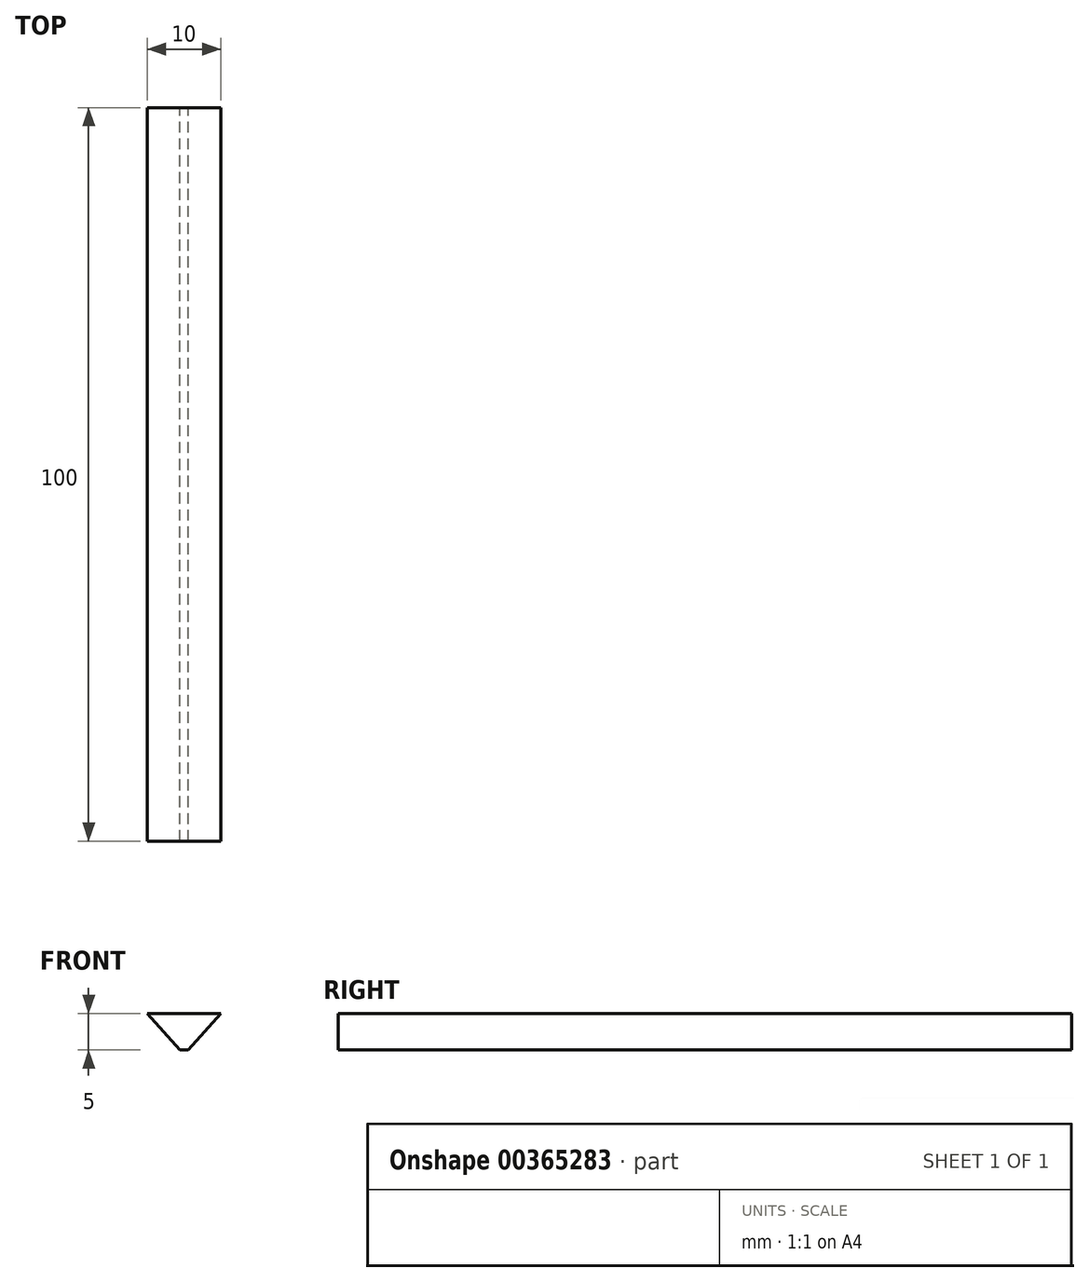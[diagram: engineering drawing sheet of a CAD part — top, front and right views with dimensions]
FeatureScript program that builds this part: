
annotation { "Feature Type Name" : "Feature", "Feature Type Description" : "" }
export const myFeature = defineFeature(function(context is Context, id is Id, definition is map)
    precondition{}
    {
        {
            var Q0;
            Q0=qCreatedBy(makeId("Front.planeOp"),FACE);
            var sketch = newSketch(context, id + "F0", { "sketchPlane" : qUnion([Q0])});
            skLineSegment(sketch, "E0", {"start": v(0, 0) * mm, "end": v(10, 0) * mm});
            skLineSegment(sketch, "E1", {"start": v(10, 0) * mm, "end": v(5.6, -5) * mm});
            skLineSegment(sketch, "E2", {"start": v(5.6, -5) * mm, "end": v(4.4, -5) * mm});
            skLineSegment(sketch, "E3", {"start": v(4.4, -5) * mm, "end": v(0, 0) * mm});
            skLineSegment(sketch, "E4", {"start": v(5, 0) * mm, "end": v(5, -5) * mm, "construction": true});
            skSolve(sketch);
        }
        {
            var Q0;
            Q0=qSketchRegion(id+"F0",true);
            extrude(context, id + "F1", {"entities" : qUnion([Q0]), "depth" : 100 * mm});
        }
    });
